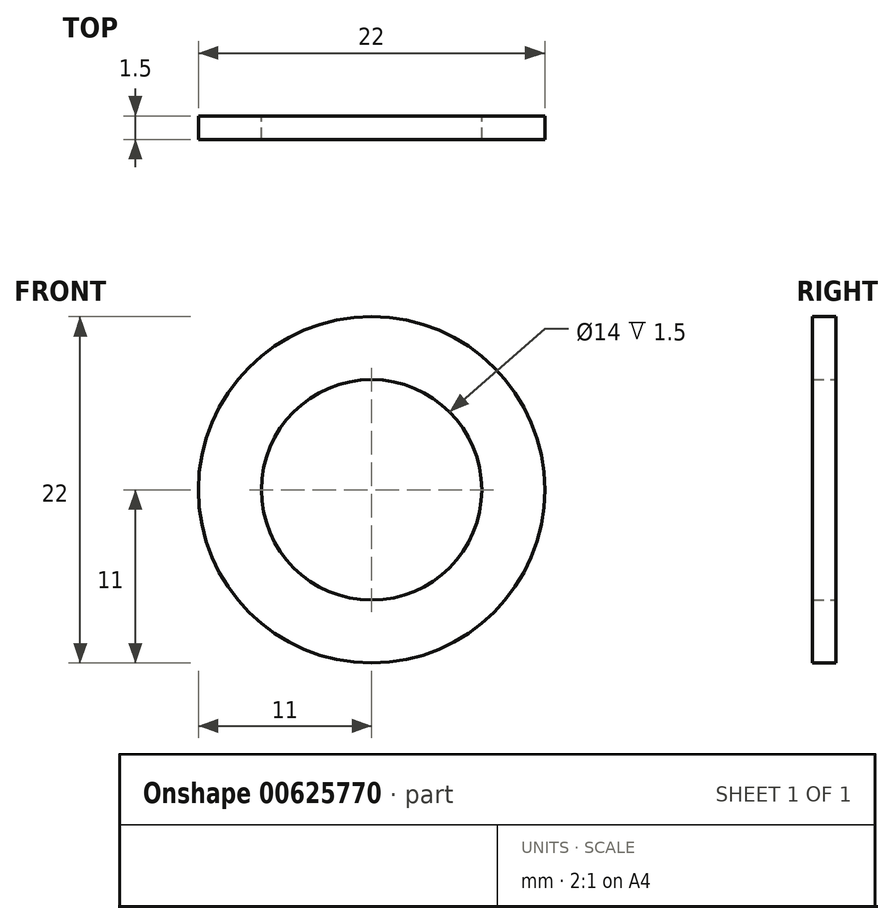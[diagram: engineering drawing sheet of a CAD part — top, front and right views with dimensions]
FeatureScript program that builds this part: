
annotation { "Feature Type Name" : "Feature", "Feature Type Description" : "" }
export const myFeature = defineFeature(function(context is Context, id is Id, definition is map)
    precondition{}
    {
        {
            var Q0;
            Q0=qCreatedBy(makeId("Front.planeOp"),FACE);
            var sketch = newSketch(context, id + "F0", { "sketchPlane" : qUnion([Q0])});
            skCircle(sketch, "E0", {"center": v(0, 0) * mm, "radius": 7 * mm});
            skCircle(sketch, "E1", {"center": v(0, 0) * mm, "radius": 11 * mm});
            skSolve(sketch);
        }
        {
            var Q0;
            Q0=makeQuery(id+"F0.imprint","IMPRINT",FACE,{"disambiguationData":[TD([[makeQuery(id+"F0.imprint","IMPRINT",EDGE,{"derivedFrom":sQuery(id+"F0.wireOp",EDGE,"E0")}),-1.0]])]});
            extrude(context, id + "F1", {"entities" : qUnion([Q0]), "depth" : 1.5 * mm, "offsetDistance" : 25 * mm});
        }
    });
